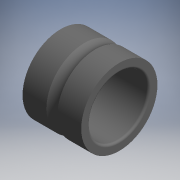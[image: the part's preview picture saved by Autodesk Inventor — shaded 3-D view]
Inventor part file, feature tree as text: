
AUTODESK INVENTOR PART (.ipt)
format: ipt  version: 2017.3 (Build 213256000, 256)  size: 149,504 bytes
history: native  units: mm (DEFAULTED — no unit token found)
features: other x84, revolve x1, sketch x1
ambient origin geometry x8: Origin, YZ Plane, XZ Plane, XY Plane, X Axis, Y Axis, Z Axis, Center Point
bodies: Solid1 (feature_tree)
feature tree (86):
  revolve  "Revolution1"  [1 undecoded]
  other  "ip_st_ir_1_1_XY"
  other  "ip_st_ir_1_1_YZ"
  other  "ip_st_ir_1_1_ZX"
  other  "ip_st_ir_1_1_X"
  other  "ip_st_ir_1_1_Y"
  other  "ip_st_ir_1_1_Z"
  other  "ip_st_ir_1_1_Center"
  other  "ip_st_ir_1_10_XY"
  other  "ip_st_ir_1_10_YZ"
  other  "ip_st_ir_1_10_ZX"
  other  "ip_st_ir_1_10_X"
  other  "ip_st_ir_1_10_Y"
  other  "ip_st_ir_1_10_Z"
  other  "ip_st_ir_1_10_Center"
  other  "ip_st_ir_1_2_XY"
  other  "ip_st_ir_1_2_YZ"
  other  "ip_st_ir_1_2_ZX"
  other  "ip_st_ir_1_2_X"
  other  "ip_st_ir_1_2_Y"
  other  "ip_st_ir_1_2_Z"
  other  "ip_st_ir_1_2_Center"
  other  "ip_st_ir_1_3_XY"
  other  "ip_st_ir_1_3_YZ"
  other  "ip_st_ir_1_3_ZX"
  other  "ip_st_ir_1_3_X"
  other  "ip_st_ir_1_3_Y"
  other  "ip_st_ir_1_3_Z"
  other  "ip_st_ir_1_3_Center"
  other  "ip_st_ir_1_4_XY"
  other  "ip_st_ir_1_4_YZ"
  other  "ip_st_ir_1_4_ZX"
  other  "ip_st_ir_1_4_X"
  other  "ip_st_ir_1_4_Y"
  other  "ip_st_ir_1_4_Z"
  other  "ip_st_ir_1_4_Center"
  other  "ip_st_ir_1_5_XY"
  other  "ip_st_ir_1_5_YZ"
  other  "ip_st_ir_1_5_ZX"
  other  "ip_st_ir_1_5_X"
  other  "ip_st_ir_1_5_Y"
  other  "ip_st_ir_1_5_Z"
  other  "ip_st_ir_1_5_Center"
  other  "ip_st_ir_1_6_XY"
  other  "ip_st_ir_1_6_YZ"
  other  "ip_st_ir_1_6_ZX"
  other  "ip_st_ir_1_6_X"
  other  "ip_st_ir_1_6_Y"
  other  "ip_st_ir_1_6_Z"
  other  "ip_st_ir_1_6_Center"
  other  "ip_st_ir_1_7_XY"
  other  "ip_st_ir_1_7_YZ"
  other  "ip_st_ir_1_7_ZX"
  other  "ip_st_ir_1_7_X"
  other  "ip_st_ir_1_7_Y"
  other  "ip_st_ir_1_7_Z"
  other  "ip_st_ir_1_7_Center"
  other  "ip_st_ir_1_8_XY"
  other  "ip_st_ir_1_8_YZ"
  other  "ip_st_ir_1_8_ZX"
  other  "ip_st_ir_1_8_X"
  other  "ip_st_ir_1_8_Y"
  other  "ip_st_ir_1_8_Z"
  other  "ip_st_ir_1_8_Center"
  other  "ip_st_ir_1_9_XY"
  other  "ip_st_ir_1_9_YZ"
  other  "ip_st_ir_1_9_ZX"
  other  "ip_st_ir_1_9_X"
  other  "ip_st_ir_1_9_Y"
  other  "ip_st_ir_1_9_Z"
  other  "ip_st_ir_1_9_Center"
  other  "ip_st_ir_1a_XY"
  other  "ip_st_ir_1a_YZ"
  other  "ip_st_ir_1a_ZX"
  other  "ip_st_ir_1a_X"
  other  "ip_st_ir_1a_Y"
  other  "ip_st_ir_1a_Z"
  other  "ip_st_ir_1a_Center"
  other  "ip_st_ir_2a_XY"
  other  "ip_st_ir_2a_YZ"
  other  "ip_st_ir_2a_ZX"
  other  "ip_st_ir_2a_X"
  other  "ip_st_ir_2a_Y"
  other  "ip_st_ir_2a_Z"
  other  "ip_st_ir_2a_Center"
  sketch  "Sketch_1"  dims[d0=360.0deg d1=0.0mm]
note: 1 required parameter value undecoded (feature->parameter linkage not recoverable at this tier; creation-order binding heuristic only, values carry confidence <= 0.55)
